# Revit family: NAU_Naughtone_Stng_Polly_Wood
name_source: partatom
category: Furniture
revit_build: Autodesk Revit 2015 (Build: 20140903_1530(x64)
units: mm (PartAtom-declared; Revit-internal decimal feet)

## types (2) — shared parameters
Assembly Code = E2020200
AssetType = Moveable
BIMObjectName = NAU_Naughtone_Seating_Polly_Wood
Category = Pr_40_50_12 Chairs, seats and benches
CodePerformance = FISP certified. ISO 14001. SCS indoor advantage gold
Color = Various
DurationUnit = year
Finish = Nonupholstered
IfcExportAs = IfcFurnishingElementType
IfcExportType = CHAIR
Keynote = Pr_40_50_12
MainColor = Various
ManufacturerAddressUK = Knaresborough Tech Park, Manse Lane, Knaresborough, HG5 8LF
ManufacturerName = Naughtone
ManufacturerURL = www.naughtone.com
Material = Wood/plastic
NBSDescription = Seating
NBSReference = 45-35-72/352
Name = Seating_Polly_Wood_Naughtone
NominalHeight = 810 mm
NominalLength = 545 mm
NominalWidth = 510 mm
ProductInformation = www.naughtone.com/portfolio-view/polly
ReplacementCost = 0.00
Shape = Rectangular
Size = 545 x 510 x 810mm
SustainabilityPerformance = FISP certified. ISO 14001. SCS indoor advantage gold
URL = www.naughtone.com
Uniclass2015Description = Chairs, seats and benches
Uniclass2015Reference = Pr_40_50_12
Uniclass2015Version = Products v1.8
Version = 1
WarrantyDurationLabor = 5
WarrantyDurationParts = 5
WarrantyDurationUnit = year

## per-type parameters (varying)
| type | Description | IsPOLLYACHWD | IsPOLLYCHWD | ModelReference |
| POLLYCHWD | Polly Wood Chair | No | Yes | Polly Wood Chair |
| POLLYACHWD | Polly Wood Chair with Arms | Yes | No | Polly Wood Chair with Arms |

note: column(s) folded — value = type name in every type: Model, ModelNumber

## geometry (parser evidence)
native form markers: Sweep x5
no freeform markers — native parametric forms only
